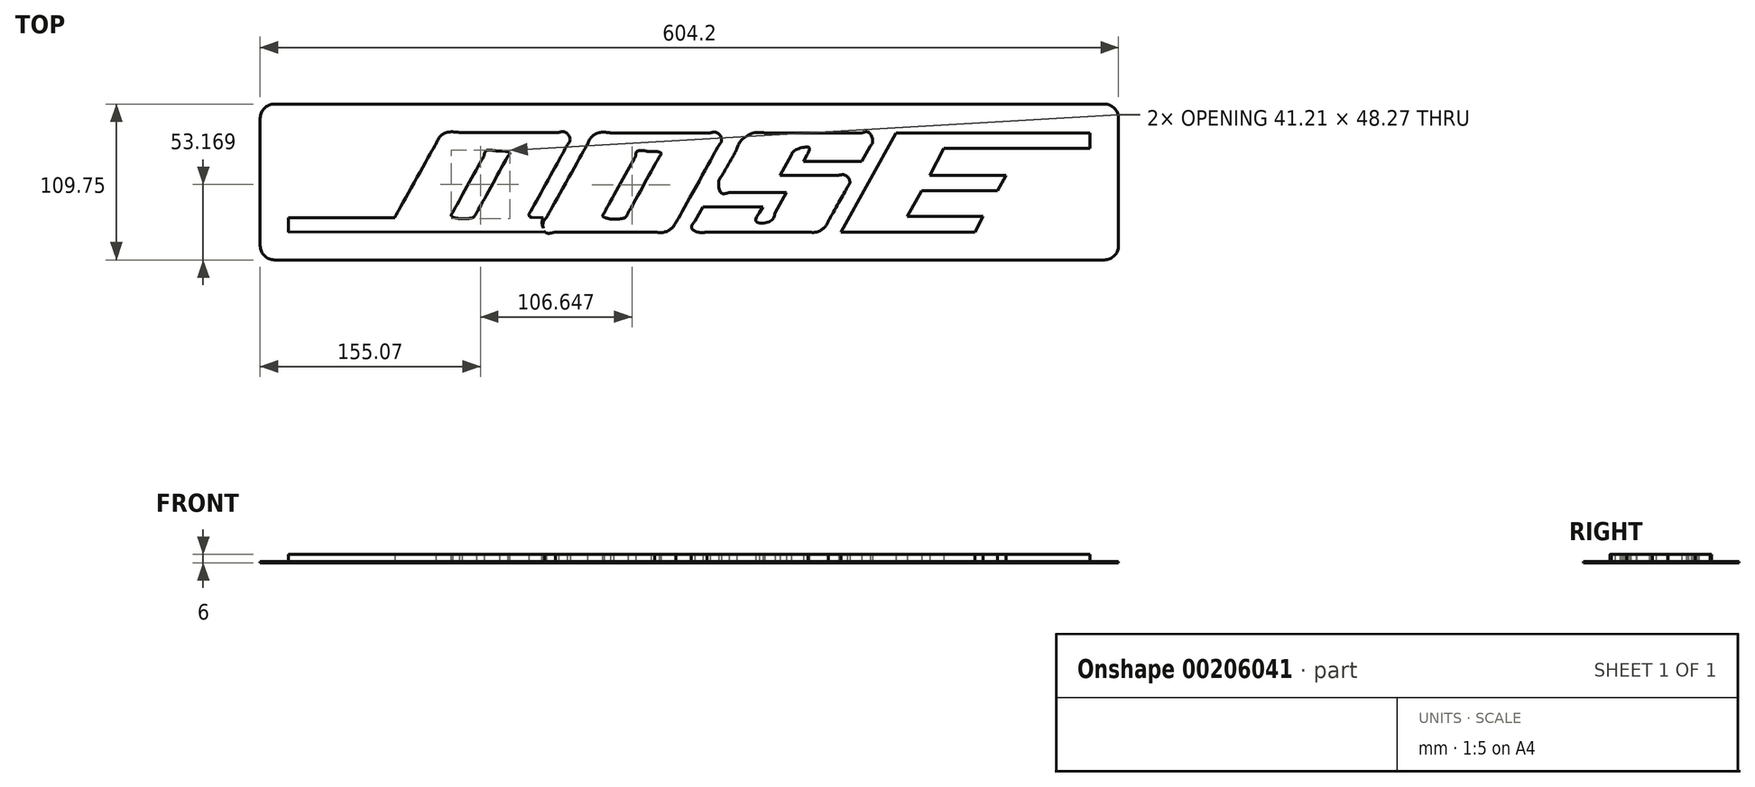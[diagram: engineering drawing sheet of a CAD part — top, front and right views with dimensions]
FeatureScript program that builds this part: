
annotation { "Feature Type Name" : "Feature", "Feature Type Description" : "" }
export const myFeature = defineFeature(function(context is Context, id is Id, definition is map)
    precondition{}
    {
        {
            var Q0;
            Q0=qCreatedBy(makeId("Top.planeOp"),FACE);
            var sketch = newSketch(context, id + "F0", { "sketchPlane" : qUnion([Q0])});
            skFitSpline(sketch, "E0", {"points": [v(76.64, 100.9) * mm, v(74.36, 100.9) * mm, v(10.5, 100.9) * mm, v(8.37, 100.9) * mm]});
            skFitSpline(sketch, "E1", {"points": [v(8.37, 100.9) * mm, v(0.77, 100.9) * mm, v(-8.16, 95.8) * mm, v(-11.43, 89.62) * mm]});
            skFitSpline(sketch, "E2", {"points": [v(-11.43, 89.62) * mm, v(-12.2, 87.94) * mm, v(-21.05, 72.24) * mm, v(-22.11, 70.41) * mm]});
            skFitSpline(sketch, "E3", {"points": [v(-22.11, 70.41) * mm, v(-24.1, 66.91) * mm, v(-22.48, 58.6) * mm, v(-16.94, 58.83) * mm]});
            skFitSpline(sketch, "E4", {"points": [v(15.53, 44.74) * mm, v(12.33, 38.8) * mm, v(2.27, 38.4) * mm, v(4.55, 44.66) * mm]});
            skFitSpline(sketch, "E5", {"points": [v(-40.92, 38.4) * mm, v(-43.3, 34) * mm, v(-37.94, 30.79) * mm, v(-32.25, 31.1) * mm]});
            skFitSpline(sketch, "E6", {"points": [v(-32.25, 31.1) * mm, v(-31.7, 31.1) * mm, v(36.65, 31.1) * mm, v(38.78, 31.1) * mm]});
            skFitSpline(sketch, "E7", {"points": [v(38.78, 31.1) * mm, v(44.65, 31.02) * mm, v(50.45, 34.37) * mm, v(52.95, 38.64) * mm]});
            skFitSpline(sketch, "E8", {"points": [v(52.95, 38.64) * mm, v(53.17, 39.02) * mm, v(65.99, 61.88) * mm, v(66.36, 62.64) * mm]});
            skFitSpline(sketch, "E9", {"points": [v(66.36, 62.64) * mm, v(68.12, 66.6) * mm, v(65, 71.02) * mm, v(60.19, 71.02) * mm]});
            skFitSpline(sketch, "E10", {"points": [v(26.95, 85.2) * mm, v(29.41, 88.55) * mm, v(39.25, 90.53) * mm, v(38.23, 85.66) * mm]});
            skLineSegment(sketch, "E11", {"start": v(6.86, 48.85) * mm, "end": v(-35.3, 48.77) * mm});
            skFitSpline(sketch, "E12", {"points": [v(82.52, 91.45) * mm, v(84.2, 94.8) * mm, v(81.52, 101.2) * mm, v(76.64, 100.9) * mm]});
            skLineSegment(sketch, "E13", {"start": v(35.43, 80.78) * mm, "end": v(76.57, 80.78) * mm});
            skLineSegment(sketch, "E14", {"start": v(100.73, 100.9) * mm, "end": v(61.73, 31.1) * mm});
            skLineSegment(sketch, "E15", {"start": v(61.73, 31.1) * mm, "end": v(156.04, 31.1) * mm});
            skLineSegment(sketch, "E16", {"start": v(156.04, 31.1) * mm, "end": v(161.77, 42) * mm});
            skLineSegment(sketch, "E17", {"start": v(161.77, 42) * mm, "end": v(108.52, 42) * mm});
            skLineSegment(sketch, "E18", {"start": v(108.52, 42) * mm, "end": v(118.8, 60.05) * mm});
            skLineSegment(sketch, "E19", {"start": v(118.8, 60.05) * mm, "end": v(172.12, 60.05) * mm});
            skLineSegment(sketch, "E20", {"start": v(172.12, 60.05) * mm, "end": v(177.93, 70.95) * mm});
            skLineSegment(sketch, "E21", {"start": v(177.93, 70.95) * mm, "end": v(124.5, 70.95) * mm});
            skLineSegment(sketch, "E22", {"start": v(124.5, 70.95) * mm, "end": v(134.19, 90.15) * mm});
            skLineSegment(sketch, "E23", {"start": v(134.19, 90.15) * mm, "end": v(237.27, 90.15) * mm});
            skLineSegment(sketch, "E24", {"start": v(237.27, 90.15) * mm, "end": v(237.27, 100.9) * mm});
            skFitSpline(sketch, "E25", {"points": [v(-30.12, 100.9) * mm, v(-32.32, 100.9) * mm, v(-98.83, 100.9) * mm, v(-100.23, 100.9) * mm]});
            skFitSpline(sketch, "E26", {"points": [v(-100.23, 100.9) * mm, v(-107.46, 101.2) * mm, v(-113.34, 98.38) * mm, v(-116.68, 92.67) * mm]});
            skFitSpline(sketch, "E27", {"points": [v(-116.68, 92.67) * mm, v(-117.75, 90.84) * mm, v(-144.89, 42.3) * mm, v(-145.47, 41.15) * mm]});
            skFitSpline(sketch, "E28", {"points": [v(-145.47, 41.15) * mm, v(-147.71, 37.5) * mm, v(-146.1, 30.79) * mm, v(-139.08, 31.1) * mm]});
            skFitSpline(sketch, "E29", {"points": [v(-139.08, 31.1) * mm, v(-135.19, 31.1) * mm, v(-71.66, 31.02) * mm, v(-69.2, 31.1) * mm]});
            skFitSpline(sketch, "E30", {"points": [v(-69.2, 31.1) * mm, v(-62.51, 30.94) * mm, v(-56.7, 34.22) * mm, v(-54.25, 37.88) * mm]});
            skFitSpline(sketch, "E31", {"points": [v(-54.25, 37.88) * mm, v(-53.22, 39.48) * mm, v(-25.09, 90.38) * mm, v(-24.1, 92.13) * mm]});
            skFitSpline(sketch, "E32", {"points": [v(-24.1, 92.13) * mm, v(-22.11, 96.1) * mm, v(-25.38, 101.13) * mm, v(-30.12, 100.9) * mm]});
            skFitSpline(sketch, "E33", {"points": [v(-82.6, 84.51) * mm, v(-83.52, 82.99) * mm, v(-104.05, 45.96) * mm, v(-104.85, 44.43) * mm]});
            skFitSpline(sketch, "E34", {"points": [v(-104.85, 44.43) * mm, v(-105.7, 42.07) * mm, v(-100.23, 40.24) * mm, v(-98.1, 40.24) * mm]});
            skFitSpline(sketch, "E35", {"points": [v(-98.1, 40.24) * mm, v(-96.33, 40.24) * mm, v(-90.24, 41.08) * mm, v(-88.04, 44.43) * mm]});
            skFitSpline(sketch, "E36", {"points": [v(-88.04, 44.43) * mm, v(-86.64, 46.72) * mm, v(-67, 82.38) * mm, v(-66.07, 83.9) * mm]});
            skFitSpline(sketch, "E37", {"points": [v(-66.07, 83.9) * mm, v(-64.71, 86.65) * mm, v(-69.67, 87.87) * mm, v(-71.8, 87.87) * mm]});
            skFitSpline(sketch, "E38", {"points": [v(-71.8, 87.87) * mm, v(-73.64, 87.87) * mm, v(-81.24, 88.1) * mm, v(-82.6, 84.51) * mm]});
            skLineSegment(sketch, "E39", {"start": v(-326.93, 41.15) * mm, "end": v(-326.93, 31.1) * mm});
            skLineSegment(sketch, "E40", {"start": v(-252.23, 41.15) * mm, "end": v(-326.93, 41.15) * mm});
            skLineSegment(sketch, "E41", {"start": v(237.27, 100.9) * mm, "end": v(100.73, 100.9) * mm});
            skLineSegment(sketch, "E42", {"start": v(82.52, 91.45) * mm, "end": v(76.57, 80.78) * mm});
            skLineSegment(sketch, "E43", {"start": v(38.23, 85.66) * mm, "end": v(35.43, 80.78) * mm});
            skLineSegment(sketch, "E44", {"start": v(26.95, 85.2) * mm, "end": v(19.05, 71.02) * mm});
            skLineSegment(sketch, "E45", {"start": v(23.31, 58.83) * mm, "end": v(15.53, 44.74) * mm});
            skLineSegment(sketch, "E46", {"start": v(-35.3, 48.77) * mm, "end": v(-40.92, 38.4) * mm});
            skLineSegment(sketch, "E47", {"start": v(19.05, 71.02) * mm, "end": v(60.19, 71.02) * mm});
            skLineSegment(sketch, "E48", {"start": v(23.31, 58.83) * mm, "end": v(-16.94, 58.83) * mm});
            skLineSegment(sketch, "E49", {"start": v(6.86, 48.85) * mm, "end": v(4.55, 44.66) * mm});
            skFitSpline(sketch, "E50", {"points": [v(-136.77, 101.16) * mm, v(-138.97, 101.16) * mm, v(-205.48, 101.16) * mm, v(-206.87, 101.16) * mm]});
            skFitSpline(sketch, "E51", {"points": [v(-206.87, 101.16) * mm, v(-214.1, 101.47) * mm, v(-219.99, 98.65) * mm, v(-223.33, 92.93) * mm]});
            skFitSpline(sketch, "E52", {"points": [v(-223.33, 92.93) * mm, v(-224.4, 91.1) * mm, v(-251.53, 42.56) * mm, v(-252.12, 41.42) * mm]});
            skFitSpline(sketch, "E53", {"points": [v(-160.9, 38.14) * mm, v(-159.87, 39.74) * mm, v(-131.74, 90.65) * mm, v(-130.74, 92.4) * mm]});
            skFitSpline(sketch, "E54", {"points": [v(-130.74, 92.4) * mm, v(-128.76, 96.36) * mm, v(-132.03, 101.4) * mm, v(-136.77, 101.16) * mm]});
            skFitSpline(sketch, "E55", {"points": [v(-189.25, 84.78) * mm, v(-190.16, 83.25) * mm, v(-210.7, 46.22) * mm, v(-211.5, 44.7) * mm]});
            skFitSpline(sketch, "E56", {"points": [v(-211.5, 44.7) * mm, v(-212.35, 42.33) * mm, v(-206.87, 40.5) * mm, v(-204.74, 40.5) * mm]});
            skFitSpline(sketch, "E57", {"points": [v(-204.74, 40.5) * mm, v(-202.98, 40.5) * mm, v(-196.89, 41.34) * mm, v(-194.68, 44.7) * mm]});
            skFitSpline(sketch, "E58", {"points": [v(-194.68, 44.7) * mm, v(-193.29, 46.98) * mm, v(-173.64, 82.64) * mm, v(-172.72, 84.17) * mm]});
            skFitSpline(sketch, "E59", {"points": [v(-172.72, 84.17) * mm, v(-171.36, 86.91) * mm, v(-176.32, 88.13) * mm, v(-178.45, 88.13) * mm]});
            skFitSpline(sketch, "E60", {"points": [v(-178.45, 88.13) * mm, v(-180.29, 88.13) * mm, v(-187.89, 88.36) * mm, v(-189.25, 84.78) * mm]});
            skLineSegment(sketch, "E61", {"start": v(-252.23, 41.15) * mm, "end": v(-252.12, 41.42) * mm});
            skLineSegment(sketch, "E62", {"start": v(-155.73, 41.27) * mm, "end": v(-147.7, 41.17) * mm});
            skFitSpline(sketch, "E63.0", {"points": [v(-147.18, 42.2) * mm, v(-147.56, 41.58) * mm, v(-148.13, 40.25) * mm, v(-148.49, 38.1) * mm, v(-148.34, 35.9) * mm, v(-147.65, 33.74) * mm, v(-146.37, 31.78) * mm, v(-144.46, 30.2) * mm, v(-141.98, 29.22) * mm, v(-140.03, 29.05) * mm, v(-139, 29.1) * mm]});
            skLineSegment(sketch, "E64", {"start": v(-326.93, 31.1) * mm, "end": v(-145.85, 31.41) * mm});
            skLineSegment(sketch, "E65", {"start": v(-145.9, 31.41) * mm, "end": v(-146.31, 31.9) * mm});
            skPoint(sketch, "E66.visualSharp", {"position": v(-159.09, 41.32) * mm});
            skArc(sketch, "E66.filletArc", {"start": v(-157.45, 44.25) * mm, "mid": v(-157.43, 42.27) * mm, "end": v(-155.73, 41.27) * mm});
            skSolve(sketch);
        }
        {
            var Q0;
            Q0 = qSketchRegion(id + "F0", true);
            extrude(context, id + "F1", {"entities" : qUnion([Q0]), "depth" : 5 * mm});
        }
        {
            var Q0;
            Q0=makeQuery(id+"F1.opExtrude","CAP_FACE",FACE,{"disambiguationData":[OSD([sQuery(id+"F0.wireOp",EDGE,"E39"),sQuery(id+"F0.wireOp",EDGE,"E40"),sQuery(id+"F0.wireOp",EDGE,"E50"),sQuery(id+"F0.wireOp",EDGE,"E51"),sQuery(id+"F0.wireOp",EDGE,"E52"),sQuery(id+"F0.wireOp",EDGE,"E53"),sQuery(id+"F0.wireOp",EDGE,"E54"),sQuery(id+"F0.wireOp",EDGE,"E55"),sQuery(id+"F0.wireOp",EDGE,"E56"),sQuery(id+"F0.wireOp",EDGE,"E57"),sQuery(id+"F0.wireOp",EDGE,"E58"),sQuery(id+"F0.wireOp",EDGE,"E59"),sQuery(id+"F0.wireOp",EDGE,"E60"),sQuery(id+"F0.wireOp",EDGE,"E61"),sQuery(id+"F0.wireOp",EDGE,"E62"),sQuery(id+"F0.wireOp",EDGE,"E63.0"),sQuery(id+"F0.wireOp",EDGE,"E64"),sQuery(id+"F0.wireOp",EDGE,"E65"),sQuery(id+"F0.wireOp",EDGE,"E66.filletArc")])],"isStart":true});
            var sketch = newSketch(context, id + "F2", { "sketchPlane" : qUnion([Q0])});
            skLineSegment(sketch, "E67.bottom", {"start": v(-346.93, -121.16) * mm, "end": v(257.27, -121.16) * mm});
            skLineSegment(sketch, "E67.top", {"start": v(-346.93, -11.41) * mm, "end": v(257.27, -11.41) * mm});
            skLineSegment(sketch, "E67.left", {"start": v(-346.93, -121.16) * mm, "end": v(-346.93, -11.41) * mm});
            skLineSegment(sketch, "E67.right", {"start": v(257.27, -121.16) * mm, "end": v(257.27, -11.41) * mm});
            skSolve(sketch);
        }
        {
            var Q0;
            Q0 = qSketchRegion(id + "F2", true);
            extrude(context, id + "F3", {"entities" : qUnion([Q0]), "depth" : 1 * mm});
        }
        {
            var Q0;
            Q0=makeQuery(id+"F3.opExtrude","SWEPT_EDGE",EDGE,{"disambiguationData":[OSD([sQuery(id+"F2.wireOp",EDGE,"E67.bottom"),sQuery(id+"F2.wireOp",EDGE,"E67.left")])]});
            var Q1;
            Q1=makeQuery(id+"F3.opExtrude","SWEPT_EDGE",EDGE,{"disambiguationData":[OSD([sQuery(id+"F2.wireOp",EDGE,"E67.top"),sQuery(id+"F2.wireOp",EDGE,"E67.left")])]});
            var Q2;
            Q2=makeQuery(id+"F3.opExtrude","SWEPT_EDGE",EDGE,{"disambiguationData":[OSD([sQuery(id+"F2.wireOp",EDGE,"E67.top"),sQuery(id+"F2.wireOp",EDGE,"E67.right")])]});
            var Q3;
            Q3=makeQuery(id+"F3.opExtrude","SWEPT_EDGE",EDGE,{"disambiguationData":[OSD([sQuery(id+"F2.wireOp",EDGE,"E67.bottom"),sQuery(id+"F2.wireOp",EDGE,"E67.right")])]});
            fillet(context, id + "F4", {"entities" : qUnion([Q0, Q1, Q2, Q3]), "radius" : 10 * mm, "tangentPropagation" : true, "allowEdgeOverflow" : false});
        }
    });
